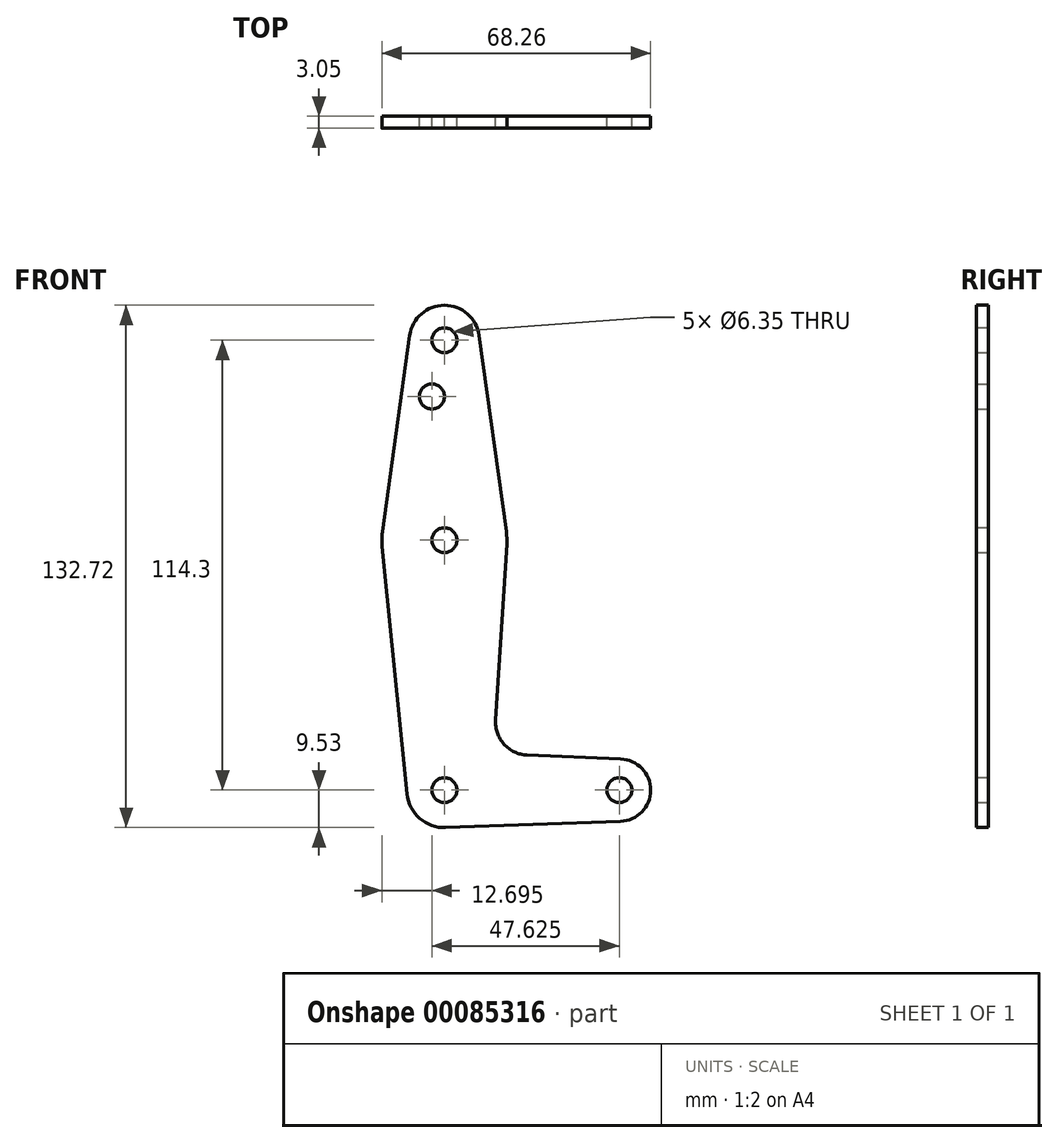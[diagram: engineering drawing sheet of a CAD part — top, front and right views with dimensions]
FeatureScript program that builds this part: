
annotation { "Feature Type Name" : "Feature", "Feature Type Description" : "" }
export const myFeature = defineFeature(function(context is Context, id is Id, definition is map)
    precondition{}
    {
        {
            var Q0;
            Q0=qCreatedBy(makeId("Front.planeOp"),FACE);
            var sketch = newSketch(context, id + "F0", { "sketchPlane" : qUnion([Q0])});
            skCircle(sketch, "E0", {"center": v(0, -63.5) * mm, "radius": 3.18 * mm});
            skCircle(sketch, "E1", {"center": v(0, -63.5) * mm, "radius": 9.53 * mm});
            skCircle(sketch, "E2", {"center": v(0, 0) * mm, "radius": 3.18 * mm});
            skCircle(sketch, "E3", {"center": v(0, 0) * mm, "radius": 15.88 * mm});
            skCircle(sketch, "E4", {"center": v(0, 50.8) * mm, "radius": 3.18 * mm});
            skCircle(sketch, "E5", {"center": v(0, 50.8) * mm, "radius": 8.9 * mm});
            skCircle(sketch, "E6", {"center": v(-3.18, 36.53) * mm, "radius": 3.18 * mm});
            skCircle(sketch, "E7", {"center": v(44.45, -63.5) * mm, "radius": 7.94 * mm});
            skLineSegment(sketch, "E8", {"start": v(-8.8, 52.02) * mm, "end": v(-15.72, 2.18) * mm});
            skLineSegment(sketch, "E9", {"start": v(-15.8, -1.59) * mm, "end": v(-9.48, -64.45) * mm});
            skLineSegment(sketch, "E10", {"start": v(15.72, 2.18) * mm, "end": v(8.8, 52.02) * mm});
            skLineSegment(sketch, "E11", {"start": v(15.84, -1) * mm, "end": v(13, -45.68) * mm});
            skLineSegment(sketch, "E12", {"start": v(21.02, -54.6) * mm, "end": v(44.78, -55.57) * mm});
            skLineSegment(sketch, "E13", {"start": v(46.51, -71.37) * mm, "end": v(0, -73.03) * mm});
            skPoint(sketch, "E14.visualSharp", {"position": v(12.46, -54.24) * mm});
            skArc(sketch, "E14.filletArc", {"start": v(13, -45.68) * mm, "mid": v(15.14, -51.82) * mm, "end": v(21.02, -54.6) * mm});
            skCircle(sketch, "E15", {"center": v(44.45, -63.5) * mm, "radius": 3.18 * mm});
            skSolve(sketch);
        }
        {
            var Q0;
            Q0=makeQuery(id+"F0.imprint","IMPRINT",FACE,{"disambiguationData":[TD([[makeQuery(id+"F0.imprint","IMPRINT",EDGE,{"derivedFrom":sQuery(id+"F0.wireOp",EDGE,"E6")}),-1.0]])]});
            var Q1;
            Q1=makeQuery(id+"F0.imprint","IMPRINT",FACE,{"disambiguationData":[TD([[makeQuery(id+"F0.imprint","IMPRINT",EDGE,{"derivedFrom":sQuery(id+"F0.wireOp",EDGE,"E4")}),-1.0]])]});
            var Q2;
            Q2=makeQuery(id+"F0.imprint","IMPRINT",FACE,{"disambiguationData":[TD([[makeQuery(id+"F0.imprint","IMPRINT",EDGE,{"derivedFrom":sQuery(id+"F0.wireOp",EDGE,"E2")}),-1.0]])]});
            var Q3;
            {var subQ9=sQuery(id+"F0.wireOp",EDGE,"E11");Q3=makeQuery(id+"F0.imprint","IMPRINT",FACE,{"disambiguationData":[TD([[makeQuery(id+"F0.imprint","IMPRINT",EDGE,{"derivedFrom":subQ9}),-1.0]])]});}
            var Q4;
            Q4=makeQuery(id+"F0.imprint","IMPRINT",FACE,{"disambiguationData":[TD([[makeQuery(id+"F0.imprint","IMPRINT",EDGE,{"derivedFrom":sQuery(id+"F0.wireOp",EDGE,"E0")}),-1.0]])]});
            var Q5;
            {var subQ0=sQuery(id+"F0.wireOp",EDGE,"E7");var subQ1=makeQuery(id+"F0.imprint","INTERSECT",VERTEX,{"derivedFrom":[subQ0,sQuery(id+"F0.wireOp",EDGE,"E12")]});Q5=makeQuery(id+"F0.imprint","IMPRINT",FACE,{"disambiguationData":[TD([[makeQuery(id+"F0.imprint","IMPRINT",EDGE,{"disambiguationData":[TD([[subQ1,-1.0]])],"derivedFrom":subQ0}),1.0]])]});}
            extrude(context, id + "F1", {"entities" : qUnion([Q0, Q1, Q2, Q3, Q4, Q5]), "depth" : 3.05 * mm});
        }
    });
